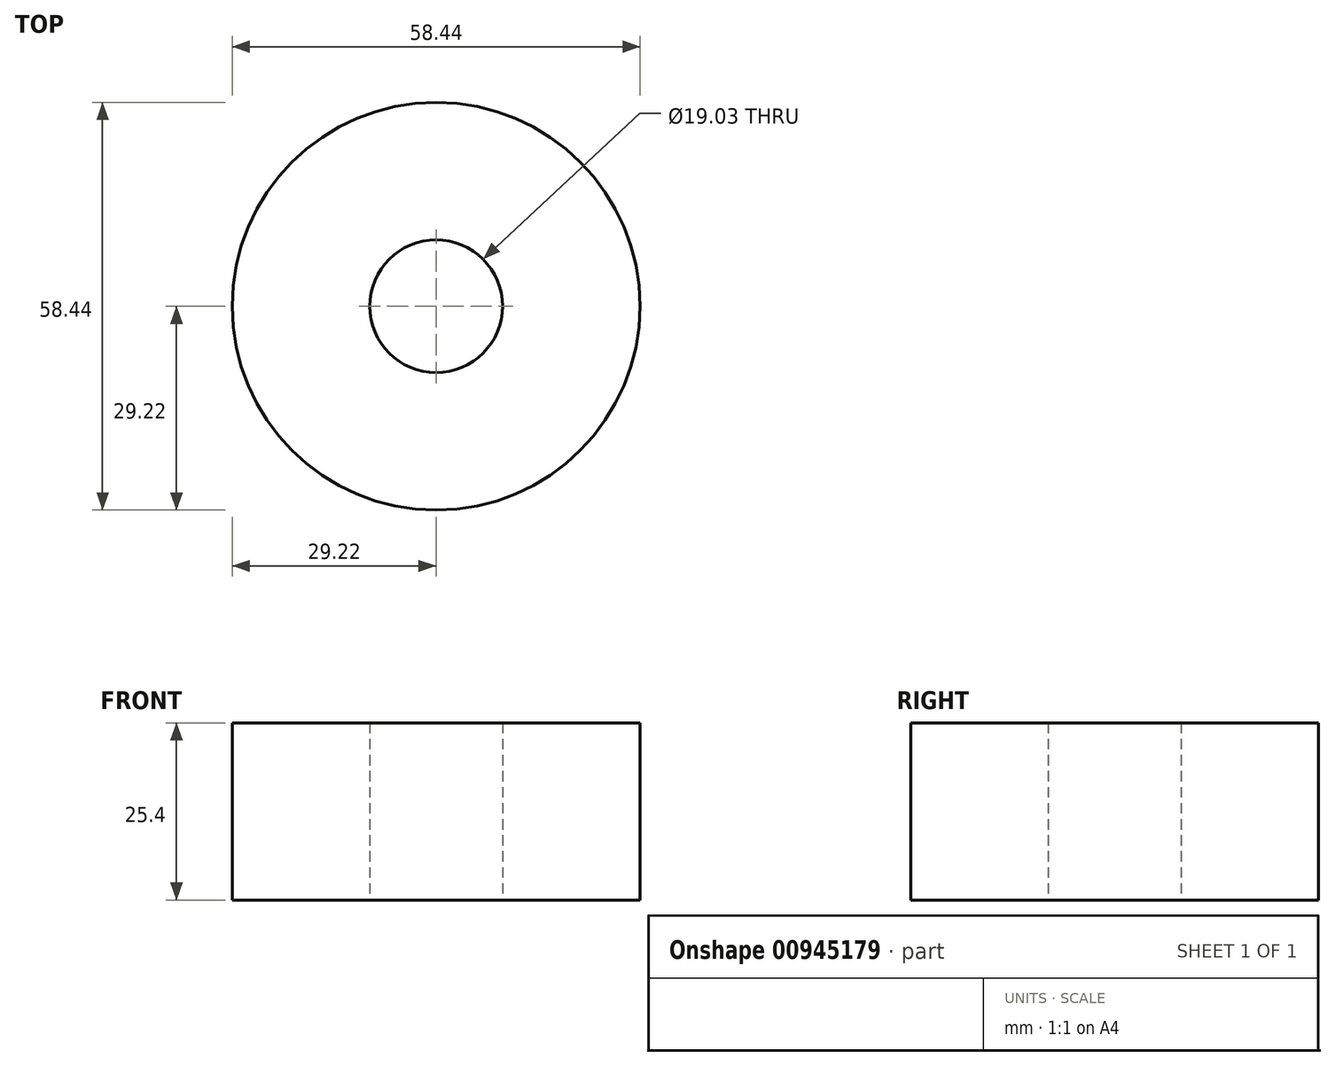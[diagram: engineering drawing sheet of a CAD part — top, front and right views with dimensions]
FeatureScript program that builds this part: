
annotation { "Feature Type Name" : "Feature", "Feature Type Description" : "" }
export const myFeature = defineFeature(function(context is Context, id is Id, definition is map)
    precondition{}
    {
        {
            var Q0;
            Q0=qCreatedBy(makeId("Top.planeOp"),FACE);
            var sketch = newSketch(context, id + "F0", { "sketchPlane" : qUnion([Q0])});
            skCircle(sketch, "E0", {"center": v(0, 0) * mm, "radius": 29.22 * mm});
            skCircle(sketch, "E1", {"center": v(0, 0) * mm, "radius": 9.51 * mm});
            skSolve(sketch);
        }
        {
            var Q0;
            Q0 = qSketchRegion(id + "F0", true);
            extrude(context, id + "F1", {"entities" : qUnion([Q0]), "depth" : 25.4 * mm, "offsetDistance" : 25.4 * mm});
        }
    });
